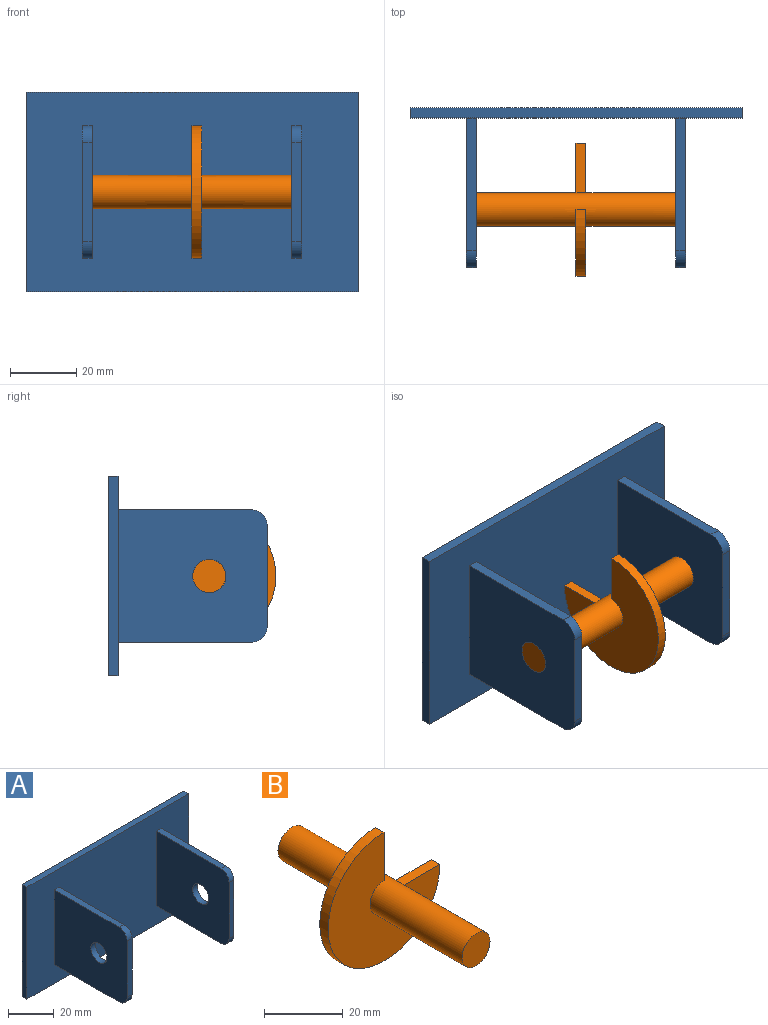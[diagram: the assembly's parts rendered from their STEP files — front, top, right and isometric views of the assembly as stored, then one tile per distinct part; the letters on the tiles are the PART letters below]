
ASSEMBLY  parts=2 mates=1
PART A: 22 faces, bbox 100x48x60 mm
  f0: plane 60x3mm, normal (1,0,0), area 180mm2, adj f1,f3,f4,f5
  f1: plane 100x3mm, normal (0,0,1), area 300mm2, adj f0,f2,f4,f5
  f2: plane 60x3mm, normal (-1,0,0), area 180mm2, adj f1,f3,f4,f5
  f3: plane 100x3mm, normal (0,0,-1), area 300mm2, adj f0,f2,f4,f5
  f4: plane 100x60mm, normal (0,-1,0), area 5760mm2, adj f0,f1,f2,f3,f6,f7,f8,f9
  f5: plane 100x60mm, normal (0,1,0), area 6000mm2, adj f0,f1,f2,f3
  f6: plane 40x3mm, normal (0,0,1), area 120mm2, adj f4,f7,f9,f21
  f7: plane 45x40mm, normal (-1,0,0), area 1710.7mm2, adj f4,f6,f8,f10,f17,f20,f21
  f8: plane 40x3mm, normal (0,0,-1), area 120mm2, adj f4,f7,f9,f20
  f9: plane 45x40mm, normal (1,0,0), area 1710.7mm2, adj f4,f6,f8,f10,f17,f20,f21
  f10: plane 30x3mm, normal (0,-1,0), area 90mm2, adj f7,f9,f20,f21
  f11: plane 45x40mm, normal (1,0,0), area 1710.7mm2, adj f4,f12,f14,f15,f16,f18,f19
  f12: plane 40x3mm, normal (0,0,1), area 120mm2, adj f4,f11,f13,f18
  f13: plane 45x40mm, normal (-1,0,0), area 1710.7mm2, adj f4,f12,f14,f15,f16,f18,f19
  f14: plane 40x3mm, normal (0,0,-1), area 120mm2, adj f4,f11,f13,f19
  f15: plane 30x3mm, normal (0,-1,0), area 90mm2, adj f11,f13,f18,f19
  f16: cylinder r=5mm len=10mm, axis (1,0,0), area 94.2mm2, adj f11,f13
  f17: cylinder r=5mm len=10mm, axis (1,0,0), area 94.2mm2, adj f7,f9
  f18: cylinder r=5mm len=5mm, axis (1,0,0), area 23.6mm2, adj f11,f12,f13,f15
  f19: cylinder r=5mm len=5mm, axis (-1,0,0), area 23.6mm2, adj f11,f13,f14,f15
  f20: cylinder r=5mm len=5mm, axis (-1,0,0), area 23.6mm2, adj f7,f8,f9,f10
  f21: cylinder r=5mm len=5mm, axis (1,0,0), area 23.6mm2, adj f6,f7,f9,f10
PART B: 8 faces, bbox 40x66x40 mm
  f0: plane 14.93x3mm, normal (1,0,0), area 44.8mm2, adj f2,f3,f4,f6
  f1: plane 15x3mm, normal (0,0,1), area 45mm2, adj f2,f3,f4,f6
  f2: cylinder r=20mm len=40mm, axis (0,1,0), area 282.9mm2, adj f0,f1,f3,f4
  f3: plane 40x40mm, normal (0,-1,0), area 884.5mm2, adj f0,f1,f2,f6
  f4: plane 40x40mm, normal (0,1,0), area 884.5mm2, adj f0,f1,f2,f6
  f5: plane 10x10mm, normal (0,-1,0), area 78.5mm2, adj f6
  f6: cylinder r=5mm len=66mm, axis (0,1,0), area 2002.9mm2, adj f0,f1,f3,f4,f5,f7
  f7: plane 10x10mm, normal (0,1,0), area 78.5mm2, adj f6
PLACE A t=(-0.3,3.1,-0.63)mm
PLACE B rot(axis=(-0.58,-0.58,-0.58),120deg) t=(2.7,-27.4,-0.63)mm
MATE revolute B.f6 <-> A.f16  axis (1,0,0) through (32.7,-27.4,-0.63)mm
